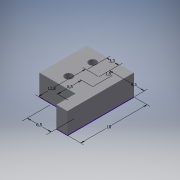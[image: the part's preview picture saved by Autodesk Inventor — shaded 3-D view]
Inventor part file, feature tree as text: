
AUTODESK INVENTOR PART (.ipt)
format: ipt  version: 2016 (Build 200138000, 138)  size: 106,496 bytes
history: native  units: mm
features: sketch x1, extrude x1, hole x1
ambient origin geometry x8: Origin, YZ Plane, XZ Plane, XY Plane, X Axis, Y Axis, Z Axis, Center Point
bodies: Solid1 (feature_tree)
feature tree (3):
  sketch  "Sketch1"  dims[d0=6.5mm d5=12.8mm d6=18.0mm d7=9.5mm d8=3.3mm d9=5.7mm d10=0.0mm d13=6.5mm d14=1.5mm d15=2.1mm d16=6.0mm d17=4.0mm d18=2.0mm d19=90.0deg d20=8.0mm d21=20.594885mm]
  extrude  "Extrusion1"  Depth=12.8mm
  hole  "Hole1"  [1 undecoded]
note: 1 required parameter value undecoded (feature->parameter linkage not recoverable at this tier; creation-order binding heuristic only, values carry confidence <= 0.55)
